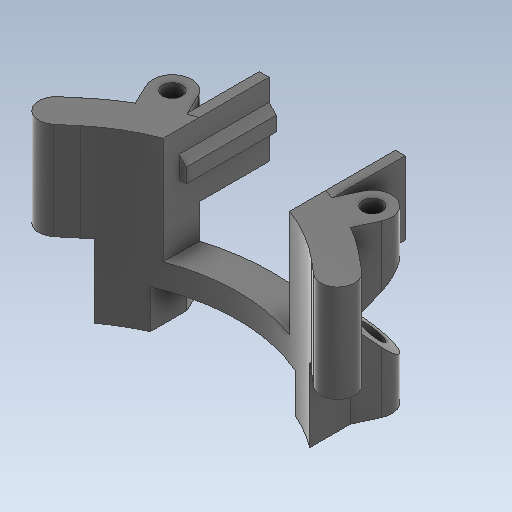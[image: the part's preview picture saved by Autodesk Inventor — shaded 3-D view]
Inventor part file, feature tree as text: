
AUTODESK INVENTOR PART (.ipt)
format: ipt  version: 2020 (Build 240168000, 168)  size: 592,896 bytes
history: native  units: mm
features: sketch x10, extrude x9, projected_geometry x7, other x2, sweep x1
ambient origin geometry x8: Origin, YZ Plane, XZ Plane, XY Plane, X Axis, Y Axis, Z Axis, Center Point
bodies: Body1 (feature_tree)
feature tree (29):
  other  "Твердое тело1"
  extrude  "Выдавливание1"  Depth=35.0mm TaperAngle=0.0deg
  sketch  "Эскиз2"
  extrude  "Выдавливание2"  Depth=4.0mm
  sweep  "Сдвиг1"
  extrude  "Выдавливание5"  Depth=8.0mm
  extrude  "Выдавливание6"  Depth=35.0mm TaperAngle=0.0deg
  extrude  "Выдавливание7"  Depth=8.5mm
  extrude  "Выдавливание8"  TaperAngle=45.0deg  [1 undecoded]
  other  "РабПлоскость1"
  extrude  "Выдавливание9"  Depth=8.5mm
  extrude  "Выдавливание10"  TaperAngle=45.0deg  [1 undecoded]
  extrude  "Выдавливание11"  TaperAngle=0.0deg  [1 undecoded]
  sketch  "Эскиз1"
  sketch  "Эскиз3"
  projected_geometry  "Спроецированная петля1"
  projected_geometry  "Спроецированная петля2"
  sketch  "3D эскиз1"
  sketch  "Эскиз4"
  sketch  "Эскиз6"
  projected_geometry  "Спроецированная петля4"
  sketch  "Эскиз7"
  projected_geometry  "Спроецированная петля5"
  sketch  "Эскиз9"
  projected_geometry  "Спроецированная петля7"
  sketch  "Эскиз11"
  projected_geometry  "Спроецированная петля8"
  sketch  "Эскиз12"
  projected_geometry  "Спроецированная петля9"
note: 3 required parameter values undecoded (feature->parameter linkage not recoverable at this tier; creation-order binding heuristic only, values carry confidence <= 0.55)
